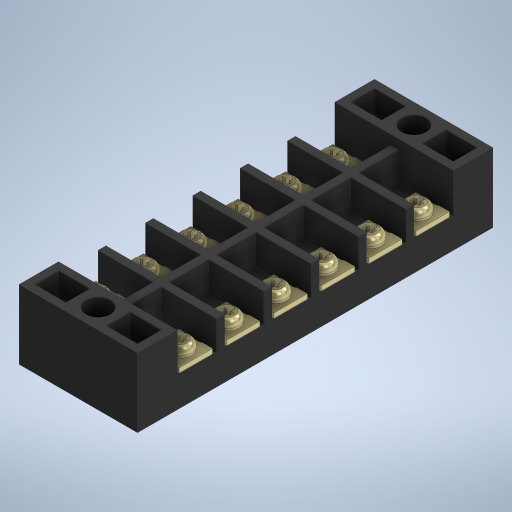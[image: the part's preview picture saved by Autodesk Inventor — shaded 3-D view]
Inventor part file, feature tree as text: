
AUTODESK INVENTOR PART (.ipt)
format: ipt  version: 2024 (Build 280153000, 153)  size: 2,194,432 bytes
history: native  units: in
note: dims shown in document units (in); Inventor stores cm internally (conversion verified against a paired STEP export)
features: sketch x10, extrude x8, plane x6, mirror x4, fillet x2, projected_geometry x1
ambient origin geometry x8: Origin, YZ Plane, XZ Plane, XY Plane, X Axis, Y Axis, Z Axis, Center Point
bodies: Solid1 (feature_tree)
feature tree (31):
  extrude  "Extrusion1"  Depth=3.6in
  extrude  "Extrusion2"  Depth=0.4in
  extrude  "Extrusion3"  Depth=0.4in
  extrude  "Extrusion4"  Depth=0.08in
  extrude  "Extrusion5"  Depth=0.08in
  fillet  "Fillet1"  Radius=0.4in
  extrude  "Extrusion6"  Depth=0.4in
  plane  "Work Plane1"
  plane  "Work Plane2"
  plane  "Work Plane3"
  plane  "Work Plane4"
  plane  "Work Plane5"
  plane  "Work Plane6"
  extrude  "Extrusion7"  Depth=0.4in
  fillet  "Fillet2"  Radius=0.08in
  mirror  "Mirror2"
  mirror  "Mirror3"
  mirror  "Mirror4"
  mirror  "Mirror5"
  sketch  "Sketch8"  dims[d17=0.04in d18=0.08in]
  sketch  "Sketch9"  dims[d19=0.4in d20=0.0in]
  extrude  "Extrusion8"  Depth=0.08in
  sketch  "Sketch1"  dims[d0=1.2in d1=3.6in]
  sketch  "Sketch2"  dims[d2=0.7in d3=0.0in d4=0.4in]
  sketch  "Sketch3"  dims[d5=0.4in d6=0.4in]
  sketch  "Sketch4"  dims[d7=0.4in d8=0.08in]
  sketch  "Sketch5"  dims[d9=0.4in d10=0.08in d11=0.4in]
  sketch  "Sketch6"  dims[d12=0.08in d13=0.4in]
  sketch  "Sketch7"  dims[d14=0.08in d15=0.4in d16=0.08in]
  projected_geometry  "Projected Loop1"
  sketch  "Sketch10"  dims[d21=0.25in d22=0.08in d23=0.08in d24=0.4in d25=0.0in d26=0.17in d27=0.34in d28=0.35in d29=0.34in d30=0.01in d31=0.01in d32=0.05in d33=0.0in d34=0.1in d35=0.0in d36=0.08in d37=0.01in d38=0.0in d39=-0.04in d40=-0.04in d41=-0.04in d42=-0.04in d43=-0.04in d44=-0.04in d45=0.095in d46=0.095in d47=0.045in d48=0.09in d49=0.02in d50=0.02in d51=0.02in d52=0.02in d53=0.02in d54=0.04in d55=0.06in d56=0.0in d57=0.005in d58=0.1in d59=0.0in]
